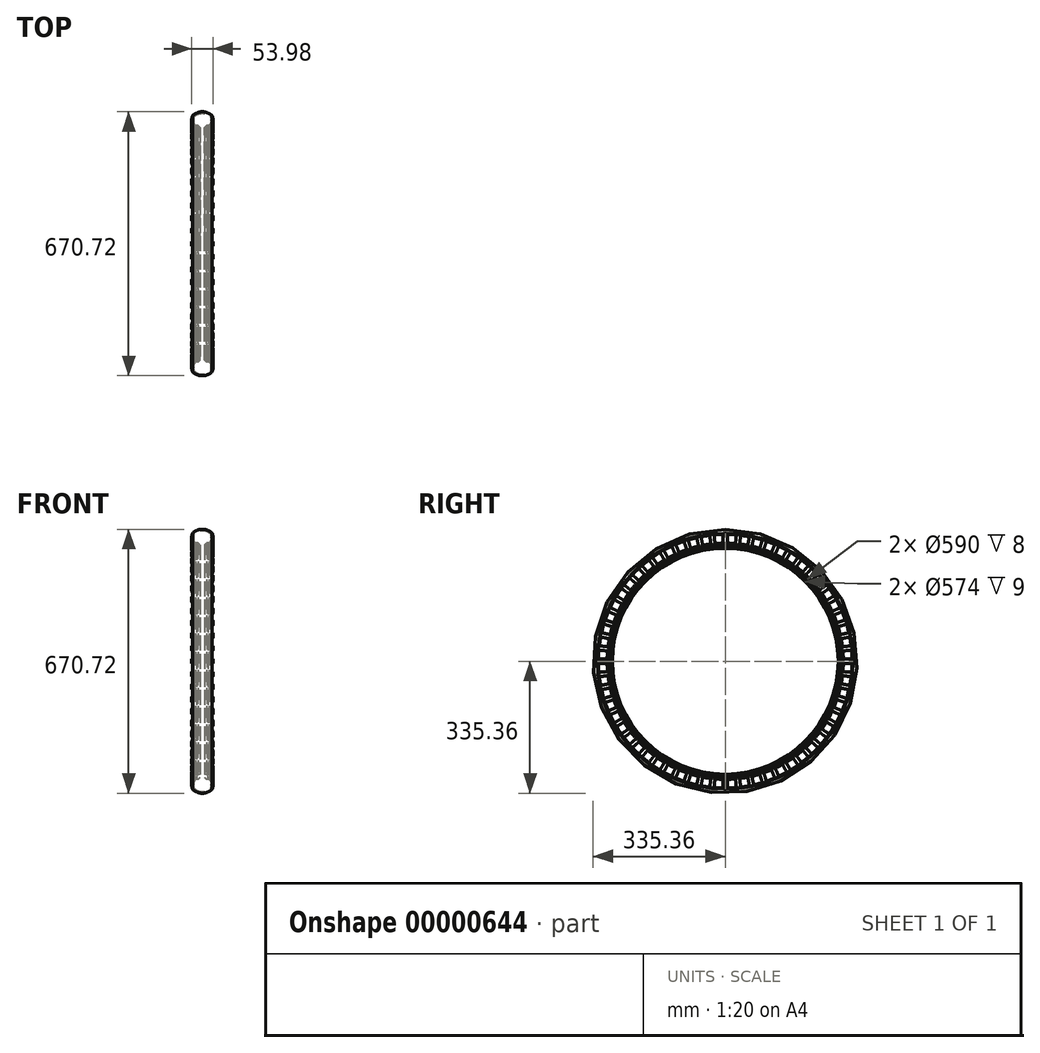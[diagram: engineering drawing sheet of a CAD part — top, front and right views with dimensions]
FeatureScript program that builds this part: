
annotation { "Feature Type Name" : "Feature", "Feature Type Description" : "" }
export const myFeature = defineFeature(function(context is Context, id is Id, definition is map)
    precondition{}
    {
        {
            var Q0;
            Q0=qCreatedBy(makeId("Front.planeOp"),FACE);
            var sketch = newSketch(context, id + "F0", { "sketchPlane" : qUnion([Q0])});
            skLineSegment(sketch, "E0", {"start": v(0, 0) * mm, "end": v(69.69, 0) * mm, "construction": true});
            skArc(sketch, "E1", {"start": v(25, 325) * mm, "mid": v(0, 335.36) * mm, "end": v(-25, 325) * mm});
            skLineSegment(sketch, "E2", {"start": v(-25, 325) * mm, "end": v(25, 325) * mm, "construction": true});
            skLineSegment(sketch, "E3", {"start": v(-17.11, 300) * mm, "end": v(-11, 300) * mm});
            skLineSegment(sketch, "E4", {"start": v(-20, 295) * mm, "end": v(-12, 295) * mm});
            skLineSegment(sketch, "E5", {"start": v(0, 300) * mm, "end": v(0, 295) * mm, "construction": true});
            skArc(sketch, "E6.0", {"start": v(22.17, 322.17) * mm, "mid": v(0, 331.36) * mm, "end": v(-22.17, 322.17) * mm});
            skLineSegment(sketch, "E7", {"start": v(22.17, 322.17) * mm, "end": v(25, 325) * mm});
            skLineSegment(sketch, "E8", {"start": v(22.17, 322.17) * mm, "end": v(26.86, 317.48) * mm, "construction": true});
            skLineSegment(sketch, "E9.0.MirrorCS", {"start": v(-22.17, 322.17) * mm, "end": v(-25, 325) * mm});
            skLineSegment(sketch, "E10", {"start": v(-20, 295) * mm, "end": v(-17.11, 300) * mm});
            skPoint(sketch, "E11.start.orphan", {"position": v(-12.5, 300) * mm});
            skLineSegment(sketch, "E12", {"start": v(-12, 295) * mm, "end": v(-12, 290) * mm});
            skLineSegment(sketch, "E13", {"start": v(-12, 290) * mm, "end": v(-15, 290) * mm});
            skLineSegment(sketch, "E14", {"start": v(-15, 290) * mm, "end": v(-15, 287) * mm});
            skLineSegment(sketch, "E15", {"start": v(-15, 287) * mm, "end": v(-6, 287) * mm});
            skLineSegment(sketch, "E16", {"start": v(-6, 287) * mm, "end": v(-6, 295) * mm});
            skLineSegment(sketch, "E17", {"start": v(-6, 295) * mm, "end": v(-11, 300) * mm});
            skLineSegment(sketch, "E18.0.MirrorCS", {"start": v(20, 295) * mm, "end": v(17.11, 300) * mm});
            skLineSegment(sketch, "E18.1.MirrorCS", {"start": v(12, 295) * mm, "end": v(12, 290) * mm});
            skLineSegment(sketch, "E18.2.MirrorCS", {"start": v(12, 290) * mm, "end": v(15, 290) * mm});
            skPoint(sketch, "E18.3.MirrorP", {"position": v(12.5, 300) * mm});
            skLineSegment(sketch, "E18.4.MirrorCS", {"start": v(17.11, 300) * mm, "end": v(11, 300) * mm});
            skLineSegment(sketch, "E18.5.MirrorCS", {"start": v(15, 287) * mm, "end": v(6, 287) * mm});
            skLineSegment(sketch, "E18.6.MirrorCS", {"start": v(6, 295) * mm, "end": v(11, 300) * mm});
            skLineSegment(sketch, "E18.7.MirrorCS", {"start": v(15, 290) * mm, "end": v(15, 287) * mm});
            skLineSegment(sketch, "E18.8.MirrorCS", {"start": v(6, 287) * mm, "end": v(6, 295) * mm});
            skLineSegment(sketch, "E19.0.MirrorCS", {"start": v(20, 295) * mm, "end": v(12, 295) * mm});
            skSolve(sketch);
        }
        {
            var Q0;
            {Q0=qUnion([makeQuery(id+"F0.imprint","IMPRINT",FACE,{"disambiguationData":[TD([[makeQuery(id+"F0.imprint","IMPRINT",EDGE,{"derivedFrom":sQuery(id+"F0.wireOp",EDGE,"E1")}),1.0]])]}),makeQuery(id+"F0.imprint","IMPRINT",FACE,{"disambiguationData":[TD([[makeQuery(id+"F0.imprint","IMPRINT",EDGE,{"derivedFrom":sQuery(id+"F0.wireOp",EDGE,"E3")}),-1.0]])]}),makeQuery(id+"F0.imprint","IMPRINT",FACE,{"disambiguationData":[TD([[makeQuery(id+"F0.imprint","IMPRINT",EDGE,{"derivedFrom":sQuery(id+"F0.wireOp",EDGE,"E18.0.MirrorCS")}),1.0]])]})]);}
            var Q1;
            Q1=sQuery(id+"F0.wireOp",EDGE,"E0");
            revolve(context, id + "F1", {"entities" : qUnion([Q0]), "axis" : qUnion([Q1]), "revolveType" : RevolveType.FULL});
        }
        {
            var Q0;
            Q0=qCreatedBy(makeId("Front.planeOp"),FACE);
            var sketch = newSketch(context, id + "F2", { "sketchPlane" : qUnion([Q0])});
            skLineSegment(sketch, "E20.0", {"start": v(-17.11, -300) * mm, "end": v(-17.11, -295) * mm});
            skLineSegment(sketch, "E21", {"start": v(-25, 325) * mm, "end": v(-22.17, 322.17) * mm});
            skArc(sketch, "E22", {"start": v(-25, 325) * mm, "mid": v(-26.58, 309.32) * mm, "end": v(-20, 295) * mm});
            skArc(sketch, "E23", {"start": v(-22.17, 322.17) * mm, "mid": v(-23.1, 310.3) * mm, "end": v(-17.11, 300) * mm});
            skPoint(sketch, "E24.orphan", {"position": v(-20, 295) * mm});
            skPoint(sketch, "E25.orphan", {"position": v(0, 0) * mm});
            skLineSegment(sketch, "E26", {"start": v(0, 0) * mm, "end": v(113.72, 0) * mm, "construction": true});
            skLineSegment(sketch, "E27", {"start": v(0, 629.27) * mm, "end": v(0, 0) * mm, "construction": true});
            skLineSegment(sketch, "E28", {"start": v(-20, 295) * mm, "end": v(-17.11, 300) * mm});
            skLineSegment(sketch, "E29.0.MirrorCS", {"start": v(25, 325) * mm, "end": v(22.17, 322.17) * mm});
            skArc(sketch, "E30.0.MirrorCS", {"start": v(25, 325) * mm, "mid": v(26.58, 309.32) * mm, "end": v(20, 295) * mm});
            skLineSegment(sketch, "E31.0.MirrorCS", {"start": v(20, 295) * mm, "end": v(17.11, 300) * mm});
            skArc(sketch, "E32.0.MirrorCS", {"start": v(22.17, 322.17) * mm, "mid": v(23.1, 310.3) * mm, "end": v(17.11, 300) * mm});
            skSolve(sketch);
        }
        {
            var Q0;
            {Q0=qUnion([makeQuery(id+"F2.imprint","IMPRINT",FACE,{"disambiguationData":[TD([[makeQuery(id+"F2.imprint","IMPRINT",EDGE,{"derivedFrom":sQuery(id+"F2.wireOp",EDGE,"E21")}),-1.0]])]}),makeQuery(id+"F2.imprint","IMPRINT",FACE,{"disambiguationData":[TD([[makeQuery(id+"F2.imprint","IMPRINT",EDGE,{"derivedFrom":sQuery(id+"F2.wireOp",EDGE,"E29.0.MirrorCS")}),1.0]])]})]);}
            var Q1;
            Q1=sQuery(id+"F2.wireOp",EDGE,"E26");
            revolve(context, id + "F3", {"entities" : qUnion([Q0]), "axis" : qUnion([Q1]), "revolveType" : RevolveType.SYMMETRIC, "angle" : 2 * degree});
        }
        {
            var Q0;
            Q0=makeQuery(id+"F3.opRevolve","CAP_EDGE",EDGE,{"disambiguationData":[OSD([sQuery(id+"F2.wireOp",EDGE,"E28")])],"isStart":false});
            var Q1;
            Q1=makeQuery(id+"F3.opRevolve","CAP_EDGE",EDGE,{"disambiguationData":[OSD([sQuery(id+"F2.wireOp",EDGE,"E28")])],"isStart":true});
            var Q2;
            Q2=makeQuery(id+"F3.opRevolve","CAP_EDGE",EDGE,{"disambiguationData":[OSD([sQuery(id+"F2.wireOp",EDGE,"E21")])],"isStart":true});
            var Q3;
            Q3=makeQuery(id+"F3.opRevolve","CAP_EDGE",EDGE,{"disambiguationData":[OSD([sQuery(id+"F2.wireOp",EDGE,"E21")])],"isStart":false});
            var Q4;
            Q4=makeQuery(id+"F3.opRevolve","CAP_EDGE",EDGE,{"disambiguationData":[OSD([sQuery(id+"F2.wireOp",EDGE,"E31.0.MirrorCS")])],"isStart":false});
            var Q5;
            Q5=makeQuery(id+"F3.opRevolve","CAP_EDGE",EDGE,{"disambiguationData":[OSD([sQuery(id+"F2.wireOp",EDGE,"E29.0.MirrorCS")])],"isStart":false});
            var Q6;
            Q6=makeQuery(id+"F3.opRevolve","CAP_EDGE",EDGE,{"disambiguationData":[OSD([sQuery(id+"F2.wireOp",EDGE,"E29.0.MirrorCS")])],"isStart":true});
            var Q7;
            Q7=makeQuery(id+"F3.opRevolve","CAP_EDGE",EDGE,{"disambiguationData":[OSD([sQuery(id+"F2.wireOp",EDGE,"E31.0.MirrorCS")])],"isStart":true});
            fillet(context, id + "F4", {"entities" : qUnion([Q0, Q1, Q2, Q3, Q4, Q5, Q6, Q7]), "radius" : 7 * mm, "tangentPropagation" : true, "allowEdgeOverflow" : false});
        }
        {
            var Q0;
            Q0=makeQuery(id+"F3.opRevolve","SWEPT_FACE",FACE,{"disambiguationData":[OSD([sQuery(id+"F2.wireOp",EDGE,"E22")])]});
            var Q1;
            {var subQ0=sQuery(id+"F2.wireOp",EDGE,"E21");Q1=makeQuery(id+"F4.opFillet","BLEND_FACE",FACE,{"disambiguationData":[OSD([subQ0]),TDD([makeQuery(id+"F3.opRevolve","CAP_EDGE",EDGE,{"disambiguationData":[OSD([subQ0])],"isStart":false})])]});}
            var Q2;
            Q2=makeQuery(id+"F3.opRevolve","CAP_FACE",FACE,{"disambiguationData":[OSD([sQuery(id+"F2.wireOp",EDGE,"E21"),sQuery(id+"F2.wireOp",EDGE,"E22"),sQuery(id+"F2.wireOp",EDGE,"E23"),sQuery(id+"F2.wireOp",EDGE,"E28")])],"isStart":false});
            var Q3;
            {var subQ0=sQuery(id+"F2.wireOp",EDGE,"E28");Q3=makeQuery(id+"F4.opFillet","BLEND_FACE",FACE,{"disambiguationData":[OSD([subQ0]),TDD([makeQuery(id+"F3.opRevolve","CAP_EDGE",EDGE,{"disambiguationData":[OSD([subQ0])],"isStart":false})])]});}
            var Q4;
            {var subQ0=sQuery(id+"F2.wireOp",EDGE,"E28");Q4=makeQuery(id+"F4.opFillet","BLEND_FACE",FACE,{"disambiguationData":[OSD([subQ0]),TDD([makeQuery(id+"F3.opRevolve","CAP_EDGE",EDGE,{"disambiguationData":[OSD([subQ0])],"isStart":true})])]});}
            var Q5;
            Q5=makeQuery(id+"F3.opRevolve","CAP_FACE",FACE,{"disambiguationData":[OSD([sQuery(id+"F2.wireOp",EDGE,"E21"),sQuery(id+"F2.wireOp",EDGE,"E22"),sQuery(id+"F2.wireOp",EDGE,"E23"),sQuery(id+"F2.wireOp",EDGE,"E28")])],"isStart":true});
            var Q6;
            {var subQ0=sQuery(id+"F2.wireOp",EDGE,"E21");Q6=makeQuery(id+"F4.opFillet","BLEND_FACE",FACE,{"disambiguationData":[OSD([subQ0]),TDD([makeQuery(id+"F3.opRevolve","CAP_EDGE",EDGE,{"disambiguationData":[OSD([subQ0])],"isStart":true})])]});}
            var Q7;
            {var subQ0=sQuery(id+"F2.wireOp",EDGE,"E31.0.MirrorCS");Q7=makeQuery(id+"F4.opFillet","BLEND_FACE",FACE,{"disambiguationData":[OSD([subQ0]),TDD([makeQuery(id+"F3.opRevolve","CAP_EDGE",EDGE,{"disambiguationData":[OSD([subQ0])],"isStart":true})])]});}
            var Q8;
            Q8=makeQuery(id+"F3.opRevolve","CAP_FACE",FACE,{"disambiguationData":[OSD([sQuery(id+"F2.wireOp",EDGE,"E29.0.MirrorCS"),sQuery(id+"F2.wireOp",EDGE,"E30.0.MirrorCS"),sQuery(id+"F2.wireOp",EDGE,"E31.0.MirrorCS"),sQuery(id+"F2.wireOp",EDGE,"E32.0.MirrorCS")])],"isStart":true});
            var Q9;
            {var subQ0=sQuery(id+"F2.wireOp",EDGE,"E29.0.MirrorCS");Q9=makeQuery(id+"F4.opFillet","BLEND_FACE",FACE,{"disambiguationData":[OSD([subQ0]),TDD([makeQuery(id+"F3.opRevolve","CAP_EDGE",EDGE,{"disambiguationData":[OSD([subQ0])],"isStart":true})])]});}
            var Q10;
            {var subQ0=sQuery(id+"F2.wireOp",EDGE,"E31.0.MirrorCS");Q10=makeQuery(id+"F4.opFillet","BLEND_FACE",FACE,{"disambiguationData":[OSD([subQ0]),TDD([makeQuery(id+"F3.opRevolve","CAP_EDGE",EDGE,{"disambiguationData":[OSD([subQ0])],"isStart":false})])]});}
            var Q11;
            Q11=makeQuery(id+"F3.opRevolve","CAP_FACE",FACE,{"disambiguationData":[OSD([sQuery(id+"F2.wireOp",EDGE,"E29.0.MirrorCS"),sQuery(id+"F2.wireOp",EDGE,"E30.0.MirrorCS"),sQuery(id+"F2.wireOp",EDGE,"E31.0.MirrorCS"),sQuery(id+"F2.wireOp",EDGE,"E32.0.MirrorCS")])],"isStart":false});
            var Q12;
            {var subQ0=sQuery(id+"F2.wireOp",EDGE,"E29.0.MirrorCS");Q12=makeQuery(id+"F4.opFillet","BLEND_FACE",FACE,{"disambiguationData":[OSD([subQ0]),TDD([makeQuery(id+"F3.opRevolve","CAP_EDGE",EDGE,{"disambiguationData":[OSD([subQ0])],"isStart":false})])]});}
            var Q13;
            Q13=makeQuery(id+"F3.opRevolve","SWEPT_FACE",FACE,{"disambiguationData":[OSD([sQuery(id+"F2.wireOp",EDGE,"E32.0.MirrorCS")])]});
            var Q14;
            Q14=makeQuery(id+"F3.opRevolve","SWEPT_FACE",FACE,{"disambiguationData":[OSD([sQuery(id+"F2.wireOp",EDGE,"E23")])]});
            var Q15;
            Q15=makeQuery(id+"F3.opRevolve","SWEPT_FACE",FACE,{"disambiguationData":[OSD([sQuery(id+"F2.wireOp",EDGE,"E30.0.MirrorCS")])]});
            var Q16;
            Q16=makeQuery(id+"F1.opRevolve","SWEPT_FACE",FACE,{"disambiguationData":[OSD([sQuery(id+"F0.wireOp",EDGE,"E4")])]});
            circularPattern(context, id + "F5", {"faces" : qUnion([Q0, Q1, Q2, Q3, Q4, Q5, Q6, Q7, Q8, Q9, Q10, Q11, Q12, Q13, Q14, Q15]), "axis" : qUnion([Q16]), "angle" : 360 * degree, "instanceCount" : 60, "equalSpace" : true, "patternType" : PatternType.FACE});
        }
    });
